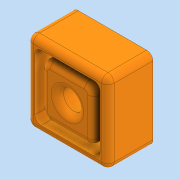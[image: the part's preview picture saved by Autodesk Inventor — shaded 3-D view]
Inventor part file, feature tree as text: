
AUTODESK INVENTOR PART (.ipt)
format: ipt  version: 2020 (Build 240168000, 168)  size: 240,128 bytes
history: native  units: mm
features: extrude x5, sketch x5, fillet x3
ambient origin geometry x8: Origin, YZ Plane, XZ Plane, XY Plane, X Axis, Y Axis, Z Axis, Center Point
bodies: Solido1 (feature_tree)
feature tree (13):
  extrude  "Estrusione1"  Depth=17.0mm
  extrude  "Estrusione2"  Depth=10.0mm TaperAngle=0.0deg
  extrude  "Estrusione6"  Depth=26.0mm
  fillet  "Raccordo3"  Radius=26.0mm
  fillet  "Raccordo8"  Radius=4.5mm
  extrude  "Estrusione9"  Depth=2.0mm
  fillet  "Raccordo9"  Radius=3.0mm
  extrude  "Estrusione10"  Depth=21.0mm
  sketch  "Schizzo1"
  sketch  "Schizzo2"
  sketch  "Schizzo12"
  sketch  "Schizzo20"
  sketch  "Schizzo21"
